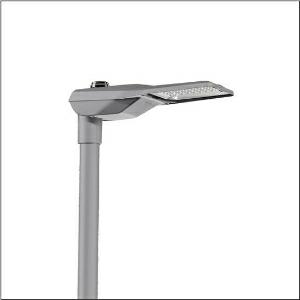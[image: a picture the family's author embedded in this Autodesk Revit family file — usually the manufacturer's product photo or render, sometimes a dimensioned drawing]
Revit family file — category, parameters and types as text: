
# Revit family: streetlight_sl_21_mini___stw1_0a_5xe6e37n08gb_9d35
name_source: partatom
category: Lighting Fixtures
units: mm (PartAtom-declared; Revit-internal decimal feet)

## family parameters
Cut with Voids When Loaded = No
Host = Face
Light Source = No
Part Type = Normal
Room Calculation Point = No
Round Connector Dimension = Use Diameter
Shared = No

## types (1)
- --- (1 x LED, 5940 lm, 40.4 W, 3000K)
    Apparent Load = 40 VA
    CIE Flux Codes = 38 75 98 100 100
    Color Rendering = 70
    Color Temperature = 3000K
    Default Elevation = 1800 mm
    Description = Streetlight SL 21 mini, mast luminaire, primary light control with lens, of PMMA, primary optical cover: cover, of toughened safety glass, transparent, light distribution: STW1.0a, light emission: direct distribution, primary light characteristic: asymmetric, installation type: side-entry, LED, 3G 1.5mm², High Power LED, rated luminous flux: 5.940lm, luminous efficacy: 147lm/W, light colour: 730, colour temperature: 3000K, control gear: NEMA (7pin), control: overheat protection, pre-setting: linear dimming characteristic, constant luminous flux control, time-dependent luminous flux control, flexible luminous flux parameterisation, mains connection: 230..240V, AC, 50/60Hz, connection cable pre-assembled, cable length: 8,5m, wiring characteristics: H07RN-F, start of lifetime: 40W, end of service life: 41W, reduction: 19W, luminaire housing, of diecast aluminium (EN AC-44300), powder-coated, Siteco® metallic grey (DB 702S), corrosivity category C5 mid according to DIN EN ISO 12944, multi-level sealing system, sealing non-destructively replaceable, inclination adjustable: 0°, 5°, 10°, 15°, length: 628mm, width: 235mm, height: 110mm, spigot size: 42mm (side-entry), mounting height: 4..8m, protection rating (complete): IP66, insulation class (complete): insulation class I (protective earthing), certification: CE, ENEC, ENEC+, VDE, impact resistance: IK10, permissible operating ambient temperature for outdoor applications: -40..+50°C, standard-compliant lighting for roads and squares, packaging unit: 1 piece

Light Distribution: STW1.0a
    Height = 110 mm
    Lamp = 1 x LED
    Lamp Light Flux = 5940 lm
    Lamp Power = 40.4 W
    Lamp count = 1
    Length = 625 mm
    Luminous efficacy = 147 lm/W
    Manufacturer = Siteco
    ModVariant = No
    Model = 5XE6E37N08GB
    Number of Poles = 1
    OnlyDefault = Yes
    Power Factor = 1
    Product Name = Streetlight SL 21 mini | STW1.0a
    Product group = mast luminaire | pylon top
    ProductGroupID = 6100
    Protection Class = Protection class I
    Protection Degree = IP 66
    RLX_Detail_Level = 1
    RLX_Emergency_Light_Flux = 0 lm
    RLX_Emergency_Type = 0
    RLX_Emergency_Type_DB = No
    RlxData = <blob elided: 25901 chars, md5=87edaeda>
    Socket = socket
    Standby Power = 0 W
    System Light Flux = 5940 lm
    System Power = 40 W
    Type Comments = factory setting: luminous flux: 100 % | dim-lin: 254 | 812 mA
    Type Image = l_1294379.jpg
    URL = http://relux.com
    VarID = @adj_157195
    Voltage = 0 V
    Weight = 0.00 kg
    Width = 234 mm

## geometry (parser evidence)
native form markers: Blend x4, Sweep x10
no freeform markers — native parametric forms only
